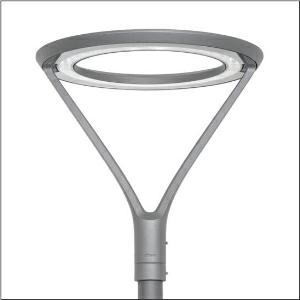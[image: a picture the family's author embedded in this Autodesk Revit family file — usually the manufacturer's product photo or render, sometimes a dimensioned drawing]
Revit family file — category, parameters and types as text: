
# Revit family: dl_r__20___p1_0a_5xa51283nr008_4ff5
name_source: partatom
category: Lighting Fixtures
units: mm (PartAtom-declared; Revit-internal decimal feet)

## family parameters
Cut with Voids When Loaded = No
Host = Face
Light Source = No
Part Type = Normal
Room Calculation Point = No
Round Connector Dimension = Use Diameter
Shared = No

## types (1)
- --- (1 x LED, 3040 lm, 23.2 W, 4000K)
    Apparent Load = 23 VA
    CIE Flux Codes = 31 71 96 100 100
    Color Rendering = 70
    Color Temperature = 4000K
    Default Elevation = 1800 mm
    Description = DL® 20, mast luminaire, primary light control with cycle path optic, highly specular, primary optical cover: cover, of toughened safety glass of clear glass with excellent transmission level, light distribution: P1.0a, light emission: direct distribution, primary light characteristic: asymmetric, installation type: post-top, LED, High Power LED, rated luminous flux: 3.050lm, luminous efficacy: 112lm/W, light colour: 740, colour temperature: 4000K, control gear: ECG Plus, control: overheat protection, power reduction, digital communication interface, constant luminous flux control, time-dependent luminous flux control, flexible luminous flux parameterisation, electronic power reduction, mains connection: 230..240V, 50/60Hz, connection cable pre-assembled, cable length: 5m, start of lifetime: 27W, end of service life: 28W, reduction: 14W, luminaire housing, upper part, of cast aluminium, powder-coated, Siteco® metallic grey (DB 702S), diameter: 690mm, height: 690mm, spigot size: 76mm (post-top), luminaire housing, of cast aluminium, powder-coated, Siteco® metallic grey (DB 702S), equipment: standard, protection rating (complete): IP66, insulation class (complete): insulation class II (safety insulation), certification: CE, ENEC, VDE, impact resistance: IK08, permissible operating ambient temperature: -25..+35°C, standard-compliant lighting for roads and squares, packaging unit: 1 piece

Light Distribution: P1.0a
    Height = 690 mm
    Lamp = 1 x LED
    Lamp Light Flux = 3040 lm
    Lamp Power = 23.2 W
    Lamp count = 1
    Length = 690 mm
    Luminous efficacy = 131 lm/W
    Manufacturer = Siteco
    ModVariant = No
    Model = 5XA51283NR008
    Number of Poles = 1
    OnlyDefault = Yes
    Power Factor = 1
    Product Name = DL® 20 | P1.0a
    Product group = mast luminaire | pylon top
    ProductGroupID = 6100
    Protection Class = Protection class II
    Protection Degree = IP 66
    RLX_Detail_Level = 1
    RLX_Emergency_Light_Flux = 0 lm
    RLX_Emergency_Type = 0
    RLX_Emergency_Type_DB = No
    RlxData = <blob elided: 206957 chars, md5=8570b86b>
    Socket = socket
    Standby Power = 0 W
    System Light Flux = 3040 lm
    System Power = 23 W
    Type Comments = factory setting: luminous flux: 100 % | dim-lin: 254 | 310 mA
    Type Image = l_1006001.jpg
    URL = http://relux.com
    VarID = @adj_027829
    Voltage = 0 V
    Weight = 0.00 kg
    Width = 0 mm  [stored 0 ft]

note: [stored X ft] marks values corroborated as IEEE doubles in the binary element streams (Revit-internal decimal feet)

## geometry (parser evidence)
native form markers: Blend x4, Sweep x11
no freeform markers — native parametric forms only
